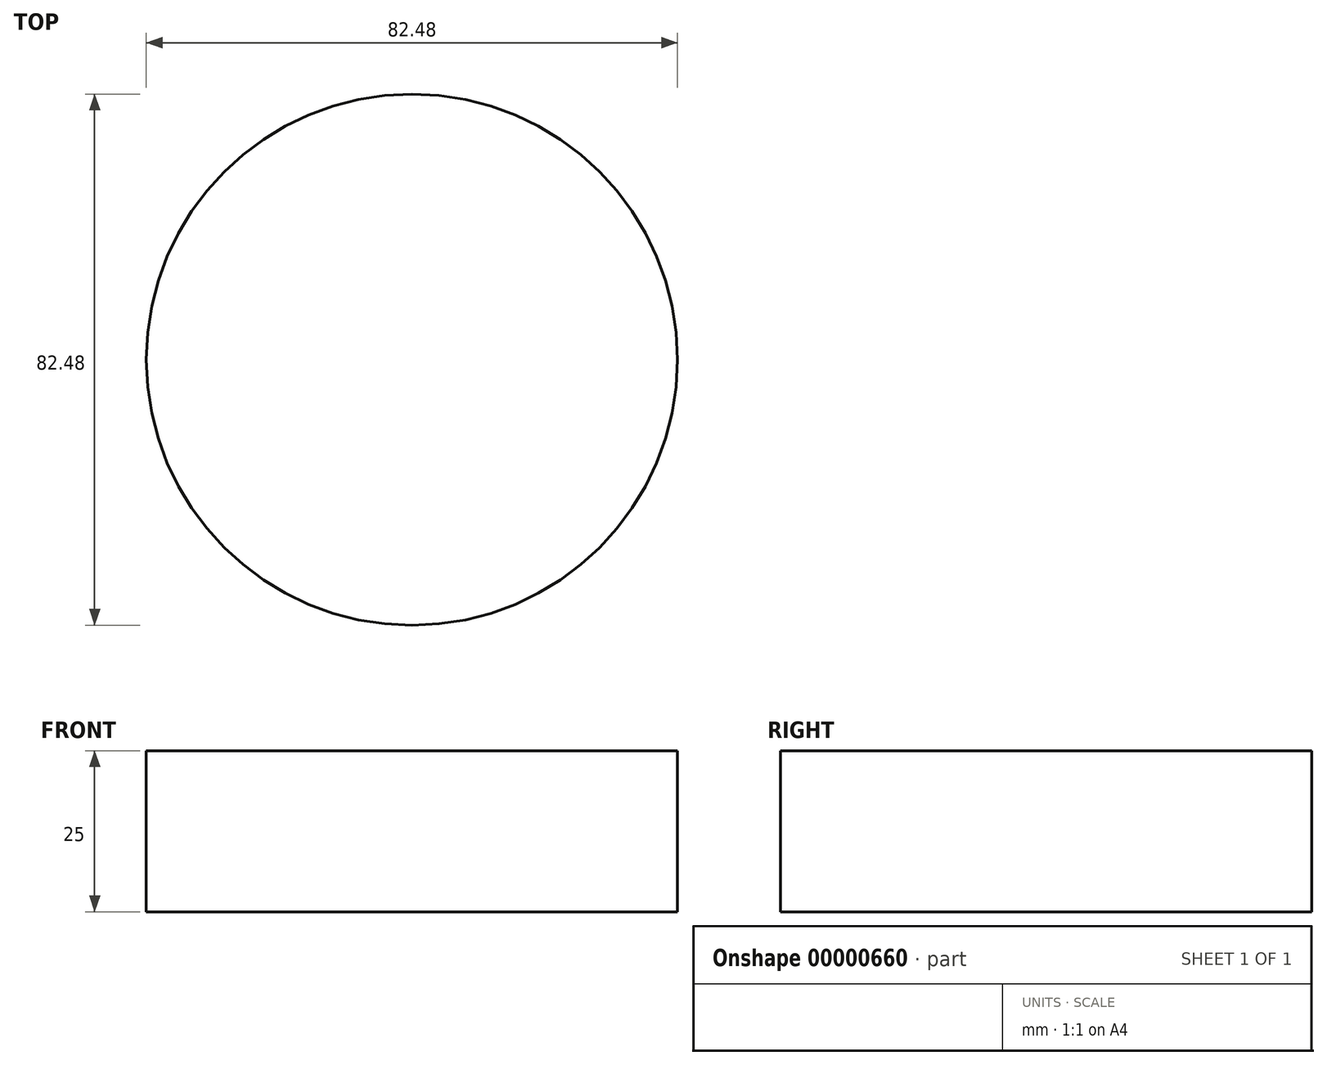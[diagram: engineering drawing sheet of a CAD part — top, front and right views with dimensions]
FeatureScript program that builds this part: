
annotation { "Feature Type Name" : "Feature", "Feature Type Description" : "" }
export const myFeature = defineFeature(function(context is Context, id is Id, definition is map)
    precondition{}
    {
        {
            var Q0;
            Q0=qCreatedBy(makeId("Top.planeOp"),FACE);
            var sketch = newSketch(context, id + "F0", { "sketchPlane" : qUnion([Q0])});
            skCircle(sketch, "E0", {"center": v(0, 0) * mm, "radius": 41.24 * mm});
            skSolve(sketch);
        }
        {
            var Q0;
            Q0=makeQuery(id+"F0.imprint","IMPRINT",FACE,{"disambiguationData":[TD([[makeQuery(id+"F0.imprint","IMPRINT",EDGE,{"derivedFrom":sQuery(id+"F0.wireOp",EDGE,"E0")}),1.0]])]});
            extrude(context, id + "F1", {"entities" : qUnion([Q0]), "depth" : 25 * mm});
        }
    });
